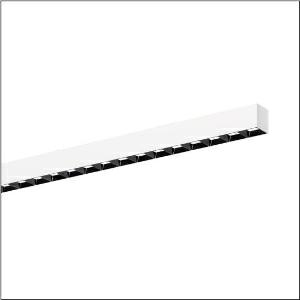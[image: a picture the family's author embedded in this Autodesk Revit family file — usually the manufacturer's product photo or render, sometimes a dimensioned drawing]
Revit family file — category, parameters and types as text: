
# Revit family: silica_r__21_51mx22tctaw_24f4
name_source: partatom
category: Lighting Fixtures
units: mm (PartAtom-declared; Revit-internal decimal feet)

## family parameters
Cut with Voids When Loaded = No
Host = Face
Light Source = No
Part Type = Normal
Room Calculation Point = No
Round Connector Dimension = Use Diameter
Shared = No

## types (1)
- --- (1 x LED, 9300 lm, 80.4 W, 6500K)
    Apparent Load = 80 VA
    CIE Flux Codes = 84 100 100 100 100
    Color Rendering = 80
    Color Temperature = 6500K
    Default Elevation = 1800 mm
    Description = Silica® 21, office luminaire, primary light control with darklight reflector, of PMMA, black, CAT 2 (L<= 3000cd/m²), light emission: direct distribution, primary light characteristic: symmetric, installation type: surface-mounted, LED, rated luminous flux: 9.300lm, luminous efficacy: 110lm/W, light colour: 8tw, colour temperature: 2700..6500K, control gear: ECG DALI, with terminal, 3+2-pole, max. 2.5mm², mains connection: 220..240V, AC, 50/60Hz, rated input power: 84.5W, luminaire housing, of aluminium, traffic white (RAL 9016), length: 3.004mm, width: 53mm, height: 53mm, protection rating (complete): IP20, insulation class (complete): insulation class I (protective earthing), certification: CE, permissible operating ambient temperature: 0..+35°C, standard: EN 50419, packaging unit: 1 piece
    Height = 0 mm  [stored 0 ft]
    Lamp = 1 x LED
    Lamp Light Flux = 9300 lm
    Lamp Power = 80.4 W
    Lamp count = 1
    Length = 3004 mm
    Luminous efficacy = 116 lm/W
    Manufacturer = Siteco
    ModVariant = No
    Model = 51MX22TCTAW
    Mounting Place = Ceiling
    Mounting Type = Recessed
    Number of Poles = 1
    OnlyDefault = Yes
    Power Factor = 1
    Product Name = Silica® 21
    Product group = office luminaire | ceiling recessed
    ProductGroupID = 401
    Protection Class = Protection class I
    Protection Degree = IP 20
    RLX_Detail_Level = 1
    RLX_Emergency_Light_Flux = 0 lm
    RLX_Emergency_Type = 0
    RLX_Emergency_Type_DB = No
    RlxData = <blob elided: 59293 chars, md5=046c76b0>
    Socket = socket
    Standby Power = 0 W
    System Light Flux = 9300 lm
    System Power = 80 W
    Type Comments = individual setting
    Type Image = l_1297779.jpg
    URL = http://relux.com
    VarID = @adj_071473
    Voltage = 0 V
    Weight = 0.00 kg
    Width = 53 mm

note: [stored X ft] marks values corroborated as IEEE doubles in the binary element streams (Revit-internal decimal feet)

## geometry (parser evidence)
native form markers: Blend x4, Sweep x10
no freeform markers — native parametric forms only
